# Revit family: 2631 Ditzel Lounge
name_source: partatom
category: Furniture
revit_build: Autodesk Revit 2017 (Build: 20171027_0315(x64)
units: mm (PartAtom-declared; Revit-internal decimal feet)

## family parameters
Always vertical = Yes
Cut with Voids When Loaded = No
OmniClass Number = 23.40.20.00
OmniClass Title = General Furniture and Specialties
Room Calculation Point = No
Shared = No
Work Plane-Based = No

## types (1)
- 2631 Ditzel Lounge
    Depth = 73 cm
    Description = The Ditzel Lounge chair was designed by Nanna Ditzel along side her husband, Jørgen Ditzel, in 1953. Nanna and Jørgen Ditzel is known for working with upholstered and enfolding shapes, that can be seen as a modern take on the traditional easy chairs and wing chairs in regards to the organic modernism.
    Design year = 1953
    Designer = Nanna Ditzel
    Height = 69,5 cm
    Item No. = 2631
    Legs = FF Oak Smoked vertical
    Manufacturer = Fredericia Furniture
    Model = Ditzel Lounge
    Seat = FF Hallingdal 110
    Seat Height = 34,5 cm
    Shell Modify = Change Shell Material in Mange -> Object Styles->Imported objects
    URL = https://www.fredericia.com
    Variation Legs = Available in other kind of wood
    Variations Upholster = Shell and Seat available in fabric
    Width = 81,5 cm

## geometry (parser evidence)
native form markers: Sweep x2
no freeform markers — native parametric forms only
